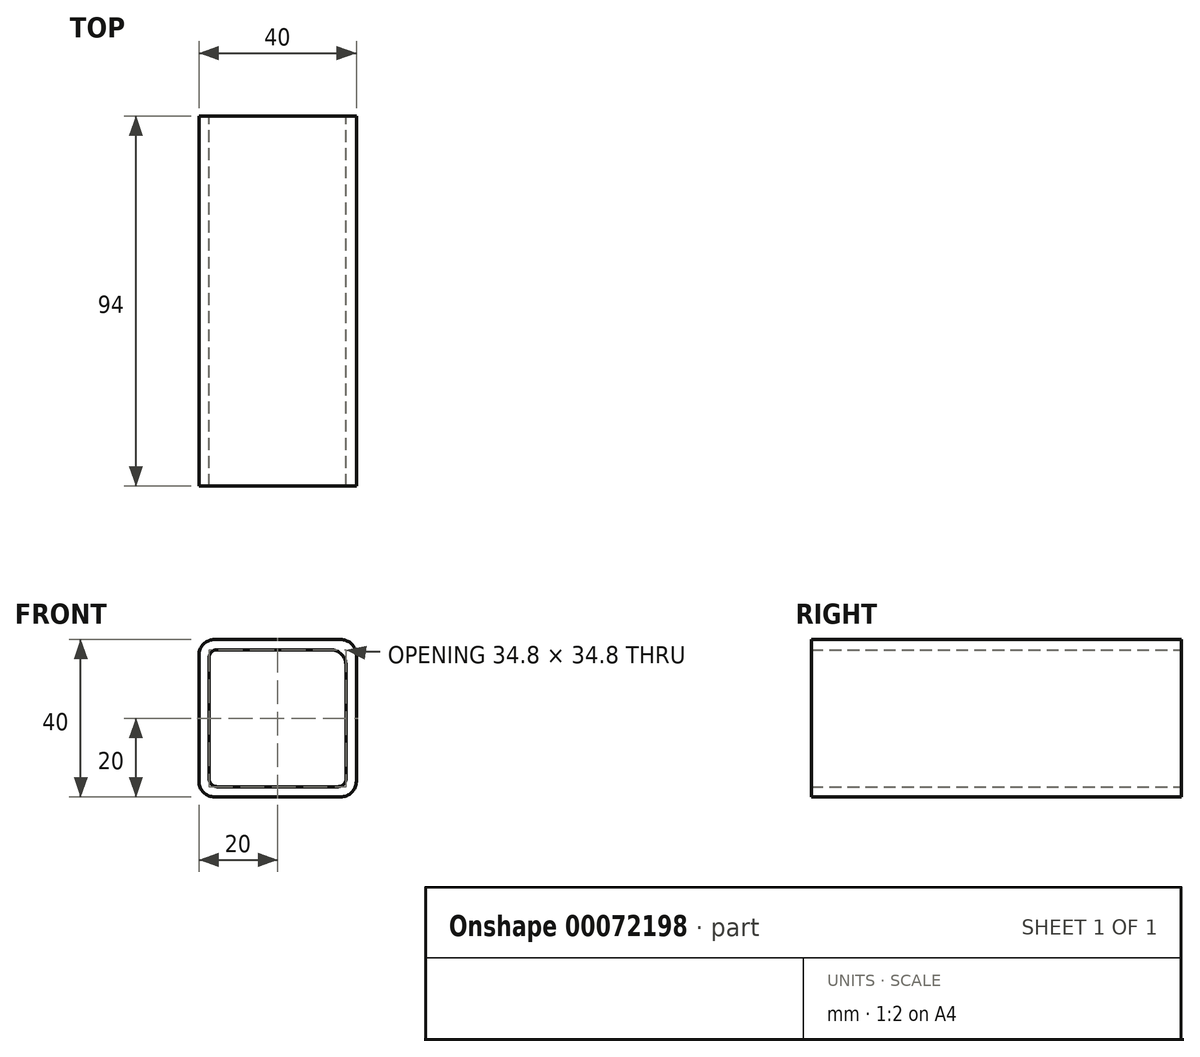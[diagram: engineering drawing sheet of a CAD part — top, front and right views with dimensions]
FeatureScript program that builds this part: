
annotation { "Feature Type Name" : "Feature", "Feature Type Description" : "" }
export const myFeature = defineFeature(function(context is Context, id is Id, definition is map)
    precondition{}
    {
        {
            var Q0;
            Q0=qCreatedBy(makeId("Front.planeOp"),FACE);
            var sketch = newSketch(context, id + "F0", { "sketchPlane" : qUnion([Q0])});
            skLineSegment(sketch, "E0.bottom", {"start": v(-20, 20) * mm, "end": v(20, 20) * mm});
            skLineSegment(sketch, "E0.top", {"start": v(-20, -20) * mm, "end": v(20, -20) * mm});
            skLineSegment(sketch, "E0.left", {"start": v(-20, 20) * mm, "end": v(-20, -20) * mm});
            skLineSegment(sketch, "E0.right", {"start": v(20, 20) * mm, "end": v(20, -20) * mm});
            skLineSegment(sketch, "E1.0", {"start": v(-17.4, 17.4) * mm, "end": v(17.4, 17.4) * mm});
            skLineSegment(sketch, "E1.1", {"start": v(-17.4, 17.4) * mm, "end": v(-17.4, -17.4) * mm});
            skLineSegment(sketch, "E1.2", {"start": v(-17.4, -17.4) * mm, "end": v(17.4, -17.4) * mm});
            skLineSegment(sketch, "E1.3", {"start": v(17.4, 17.4) * mm, "end": v(17.4, -17.4) * mm});
            skSolve(sketch);
        }
        {
            var Q0;
            Q0=makeQuery(id+"F0.imprint","IMPRINT",FACE,{"disambiguationData":[TD([[makeQuery(id+"F0.imprint","IMPRINT",EDGE,{"derivedFrom":sQuery(id+"F0.wireOp",EDGE,"E0.bottom")}),-1.0]])]});
            var Q1;
            Q1=sQuery(id+"F0.wireOp",EDGE,"E0.bottom");
            var Q2;
            Q2=sQuery(id+"F0.wireOp",EDGE,"E0.top");
            var Q3;
            Q3=sQuery(id+"F0.wireOp",EDGE,"E0.left");
            var Q4;
            Q4=sQuery(id+"F0.wireOp",EDGE,"E0.right");
            var Q5;
            Q5=sQuery(id+"F0.wireOp",EDGE,"E1.0");
            var Q6;
            Q6=sQuery(id+"F0.wireOp",EDGE,"E1.1");
            var Q7;
            Q7=sQuery(id+"F0.wireOp",EDGE,"E1.2");
            var Q8;
            Q8=sQuery(id+"F0.wireOp",EDGE,"E1.3");
            extrude(context, id + "F1", {"entities" : qUnion([Q0]), "surfaceEntities" : qUnion([Q1, Q2, Q3, Q4, Q5, Q6, Q7, Q8]), "depth" : 94 * mm});
        }
        {
            var Q0;
            Q0=makeQuery(id+"F1.opExtrude","SWEPT_EDGE",EDGE,{"disambiguationData":[OSD([sQuery(id+"F0.wireOp",VERTEX,"E0.right.start")])]});
            var Q1;
            Q1=makeQuery(id+"F1.opExtrude","SWEPT_EDGE",EDGE,{"disambiguationData":[OSD([sQuery(id+"F0.wireOp",VERTEX,"E0.left.start")])]});
            var Q2;
            Q2=makeQuery(id+"F1.opExtrude","SWEPT_EDGE",EDGE,{"disambiguationData":[OSD([sQuery(id+"F0.wireOp",VERTEX,"E0.right.end")])]});
            var Q3;
            Q3=makeQuery(id+"F1.opExtrude","SWEPT_EDGE",EDGE,{"disambiguationData":[OSD([sQuery(id+"F0.wireOp",VERTEX,"E0.left.end")])]});
            var Q4;
            Q4=makeQuery(id+"F1.opExtrude","SWEPT_EDGE",EDGE,{"disambiguationData":[OSD([sQuery(id+"F0.wireOp",EDGE,"E1.0"),sQuery(id+"F0.wireOp",EDGE,"E1.3")])]});
            var Q5;
            Q5=makeQuery(id+"F1.opExtrude","SWEPT_EDGE",EDGE,{"disambiguationData":[OSD([sQuery(id+"F0.wireOp",EDGE,"E0.bottom"),sQuery(id+"F0.wireOp",EDGE,"E0.left")])]});
            var Q6;
            Q6=makeQuery(id+"F1.opExtrude","SWEPT_EDGE",EDGE,{"disambiguationData":[OSD([sQuery(id+"F0.wireOp",EDGE,"E0.top"),sQuery(id+"F0.wireOp",EDGE,"E0.right")])]});
            var Q7;
            Q7=makeQuery(id+"F1.opExtrude","SWEPT_EDGE",EDGE,{"disambiguationData":[OSD([sQuery(id+"F0.wireOp",EDGE,"E0.top"),sQuery(id+"F0.wireOp",EDGE,"E0.left")])]});
            var Q8;
            Q8=makeQuery(id+"F1.opExtrude","SWEPT_EDGE",EDGE,{"disambiguationData":[OSD([sQuery(id+"F0.wireOp",EDGE,"E0.bottom"),sQuery(id+"F0.wireOp",EDGE,"E0.right")])]});
            fillet(context, id + "F2", {"entities" : qUnion([Q0, Q1, Q2, Q3, Q4, Q5, Q6, Q7, Q8]), "radius" : 4 * mm, "tangentPropagation" : true, "allowEdgeOverflow" : false});
        }
        {
            var Q0;
            Q0=makeQuery(id+"F1.opExtrude","SWEPT_EDGE",EDGE,{"disambiguationData":[OSD([sQuery(id+"F0.wireOp",VERTEX,"E1.1.start")])]});
            var Q1;
            Q1=makeQuery(id+"F1.opExtrude","SWEPT_EDGE",EDGE,{"disambiguationData":[OSD([sQuery(id+"F0.wireOp",VERTEX,"E1.2.start")])]});
            var Q2;
            Q2=makeQuery(id+"F1.opExtrude","SWEPT_EDGE",EDGE,{"disambiguationData":[OSD([sQuery(id+"F0.wireOp",VERTEX,"E1.3.end")])]});
            var Q3;
            Q3=makeQuery(id+"F1.opExtrude","SWEPT_EDGE",EDGE,{"disambiguationData":[OSD([sQuery(id+"F0.wireOp",VERTEX,"E1.3.start")])]});
            var Q4;
            Q4=makeQuery(id+"F1.opExtrude","SWEPT_EDGE",EDGE,{"disambiguationData":[OSD([sQuery(id+"F0.wireOp",EDGE,"E1.2"),sQuery(id+"F0.wireOp",EDGE,"E1.3")])]});
            var Q5;
            Q5=makeQuery(id+"F1.opExtrude","SWEPT_EDGE",EDGE,{"disambiguationData":[OSD([sQuery(id+"F0.wireOp",EDGE,"E1.1"),sQuery(id+"F0.wireOp",EDGE,"E1.2")])]});
            var Q6;
            Q6=makeQuery(id+"F1.opExtrude","SWEPT_EDGE",EDGE,{"disambiguationData":[OSD([sQuery(id+"F0.wireOp",EDGE,"E1.0"),sQuery(id+"F0.wireOp",EDGE,"E1.1")])]});
            fillet(context, id + "F3", {"entities" : qUnion([Q0, Q1, Q2, Q3, Q4, Q5, Q6]), "radius" : 2 * mm, "tangentPropagation" : true, "allowEdgeOverflow" : false});
        }
    });
